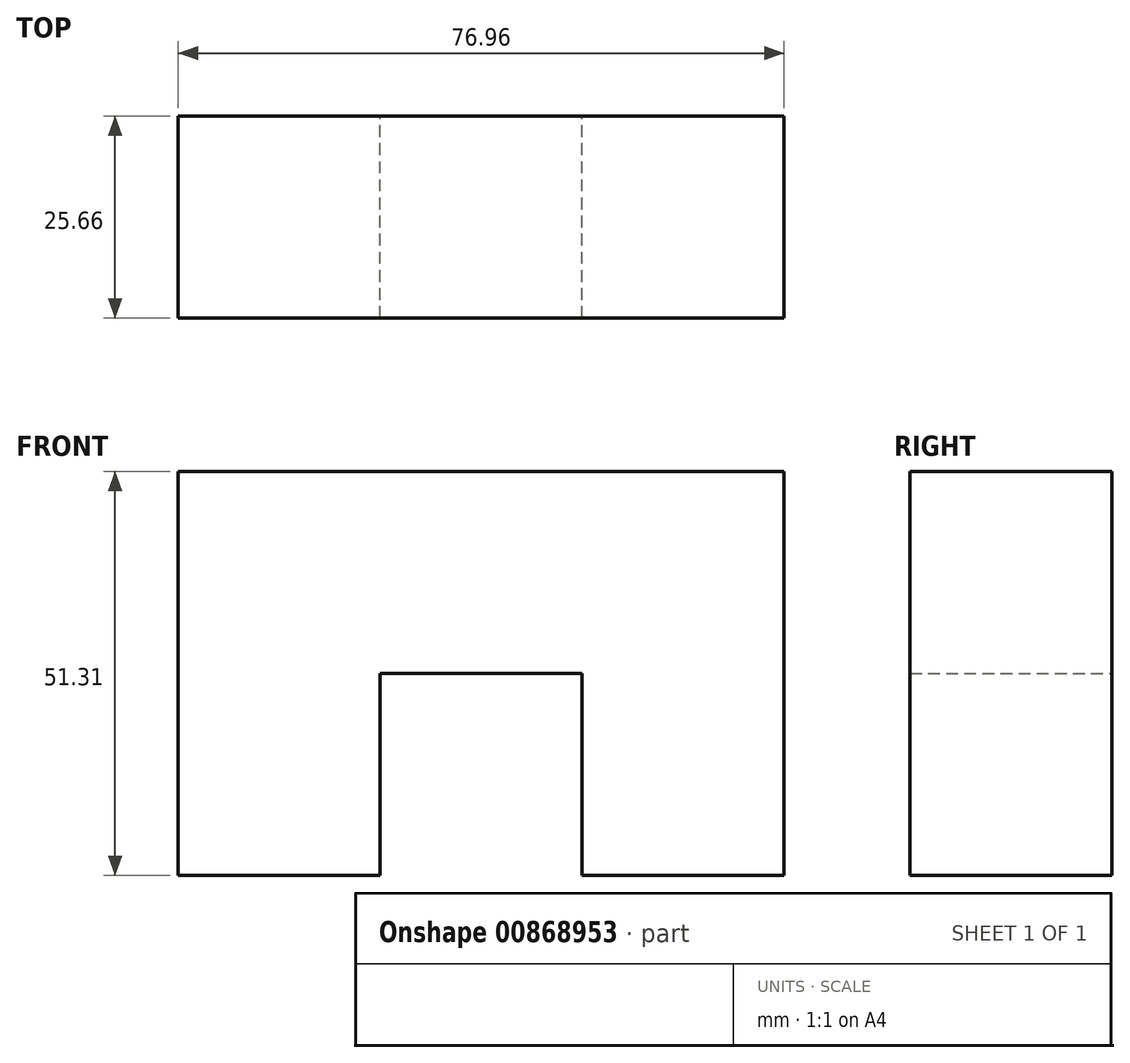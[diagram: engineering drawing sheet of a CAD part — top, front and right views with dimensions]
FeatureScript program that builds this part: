
annotation { "Feature Type Name" : "Feature", "Feature Type Description" : "" }
export const myFeature = defineFeature(function(context is Context, id is Id, definition is map)
    precondition{}
    {
        {
            var Q0;
            Q0=qCreatedBy(makeId("Front.planeOp"),FACE);
            var sketch = newSketch(context, id + "F0", { "sketchPlane" : qUnion([Q0])});
            skLineSegment(sketch, "E0", {"start": v(-54.12, 15.56) * mm, "end": v(22.84, 15.56) * mm});
            skLineSegment(sketch, "E1", {"start": v(22.84, 15.56) * mm, "end": v(22.84, -35.75) * mm});
            skLineSegment(sketch, "E2", {"start": v(22.84, -35.75) * mm, "end": v(-2.81, -35.75) * mm});
            skLineSegment(sketch, "E3", {"start": v(-2.81, -35.75) * mm, "end": v(-2.81, -10.1) * mm});
            skLineSegment(sketch, "E4", {"start": v(-2.81, -10.1) * mm, "end": v(-28.47, -10.1) * mm});
            skLineSegment(sketch, "E5", {"start": v(-28.47, -10.1) * mm, "end": v(-28.47, -35.75) * mm});
            skLineSegment(sketch, "E6", {"start": v(-28.47, -35.75) * mm, "end": v(-54.12, -35.75) * mm});
            skLineSegment(sketch, "E7", {"start": v(-54.12, -35.75) * mm, "end": v(-54.12, 15.56) * mm});
            skSolve(sketch);
        }
        {
            var Q0;
            Q0=makeQuery(id+"F0.imprint","IMPRINT",FACE,{"disambiguationData":[TD([[makeQuery(id+"F0.imprint","IMPRINT",EDGE,{"derivedFrom":sQuery(id+"F0.wireOp",EDGE,"E0")}),-1.0]])]});
            extrude(context, id + "F1", {"entities" : qUnion([Q0]), "endBound" : BoundingType.SYMMETRIC, "depth" : 25.65 * mm, "offsetDistance" : 25.4 * mm});
        }
    });
